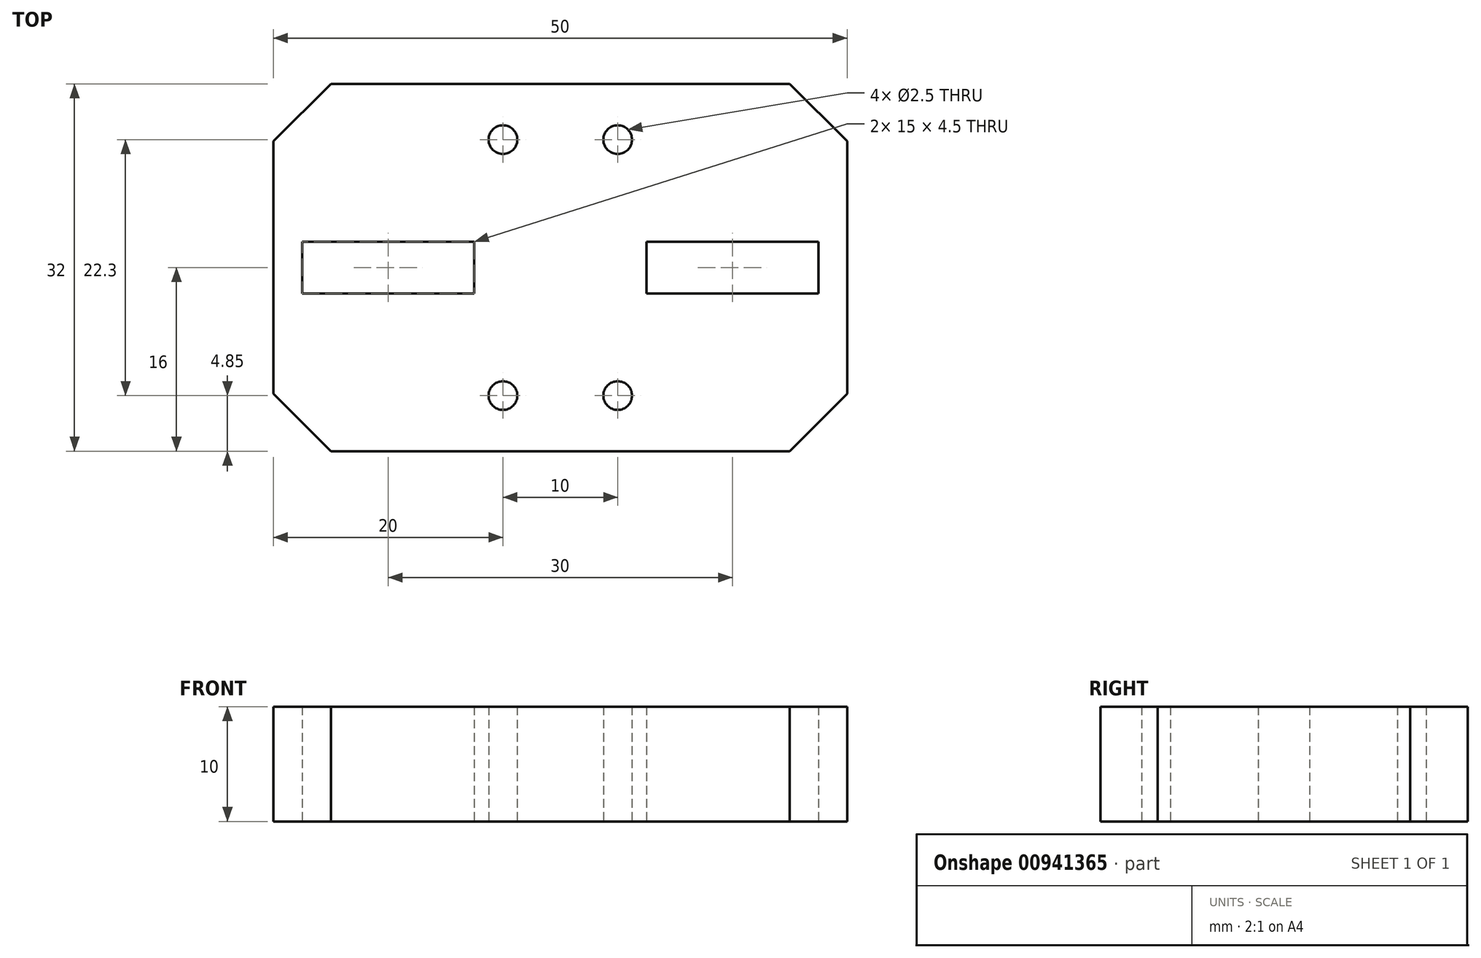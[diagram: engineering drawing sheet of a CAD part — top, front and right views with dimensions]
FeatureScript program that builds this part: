
annotation { "Feature Type Name" : "Feature", "Feature Type Description" : "" }
export const myFeature = defineFeature(function(context is Context, id is Id, definition is map)
    precondition{}
    {
        {
            var Q0;
            Q0=qCreatedBy(makeId("Top.planeOp"),FACE);
            var sketch = newSketch(context, id + "F0", { "sketchPlane" : qUnion([Q0])});
            skLineSegment(sketch, "E0.bottom", {"start": v(0, 0) * mm, "end": v(50, 0) * mm});
            skLineSegment(sketch, "E0.top", {"start": v(0, 32) * mm, "end": v(50, 32) * mm});
            skLineSegment(sketch, "E0.left", {"start": v(0, 0) * mm, "end": v(0, 32) * mm});
            skLineSegment(sketch, "E0.right", {"start": v(50, 0) * mm, "end": v(50, 32) * mm});
            skLineSegment(sketch, "E1", {"start": v(0, 16) * mm, "end": v(50, 16) * mm, "construction": true});
            skLineSegment(sketch, "E2.bottom", {"start": v(17.5, 18.25) * mm, "end": v(2.5, 18.25) * mm});
            skLineSegment(sketch, "E2.top", {"start": v(17.5, 13.75) * mm, "end": v(2.5, 13.75) * mm});
            skLineSegment(sketch, "E2.left", {"start": v(17.5, 18.25) * mm, "end": v(17.5, 13.75) * mm});
            skLineSegment(sketch, "E2.right", {"start": v(2.5, 18.25) * mm, "end": v(2.5, 13.75) * mm});
            skLineSegment(sketch, "E3", {"start": v(25, 32) * mm, "end": v(25, 0) * mm, "construction": true});
            skCircle(sketch, "E4", {"center": v(20, 27.15) * mm, "radius": 1.25 * mm});
            skCircle(sketch, "E5.MirrorC", {"center": v(30, 27.15) * mm, "radius": 1.25 * mm});
            skCircle(sketch, "E6.MirrorC", {"center": v(20, 4.85) * mm, "radius": 1.25 * mm});
            skCircle(sketch, "E7.MirrorC", {"center": v(30, 4.85) * mm, "radius": 1.25 * mm});
            skLineSegment(sketch, "E8.MirrorCS", {"start": v(32.5, 18.25) * mm, "end": v(32.5, 13.75) * mm});
            skLineSegment(sketch, "E9.MirrorCS", {"start": v(32.5, 18.25) * mm, "end": v(47.5, 18.25) * mm});
            skLineSegment(sketch, "E10.MirrorCS", {"start": v(47.5, 18.25) * mm, "end": v(47.5, 13.75) * mm});
            skLineSegment(sketch, "E11.MirrorCS", {"start": v(32.5, 13.75) * mm, "end": v(47.5, 13.75) * mm});
            skPoint(sketch, "E12", {"position": v(2.5, 16) * mm});
            skSolve(sketch);
        }
        {
            var Q0;
            Q0=makeQuery(id+"F0.imprint","IMPRINT",FACE,{"disambiguationData":[TD([[makeQuery(id+"F0.imprint","IMPRINT",EDGE,{"derivedFrom":sQuery(id+"F0.wireOp",EDGE,"E0.bottom")}),1.0]])]});
            extrude(context, id + "F1", {"entities" : qUnion([Q0]), "depth" : 10 * mm, "offsetDistance" : 25 * mm});
        }
        {
            var Q0;
            Q0=makeQuery(id+"F1.opExtrude","SWEPT_EDGE",EDGE,{"disambiguationData":[OSD([sQuery(id+"F0.wireOp",EDGE,"E0.bottom"),sQuery(id+"F0.wireOp",EDGE,"E0.left")])]});
            var Q1;
            Q1=makeQuery(id+"F1.opExtrude","SWEPT_EDGE",EDGE,{"disambiguationData":[OSD([sQuery(id+"F0.wireOp",EDGE,"E0.bottom"),sQuery(id+"F0.wireOp",EDGE,"E0.right")])]});
            var Q2;
            Q2=makeQuery(id+"F1.opExtrude","SWEPT_EDGE",EDGE,{"disambiguationData":[OSD([sQuery(id+"F0.wireOp",EDGE,"E0.top"),sQuery(id+"F0.wireOp",EDGE,"E0.right")])]});
            var Q3;
            Q3=makeQuery(id+"F1.opExtrude","SWEPT_EDGE",EDGE,{"disambiguationData":[OSD([sQuery(id+"F0.wireOp",EDGE,"E0.top"),sQuery(id+"F0.wireOp",EDGE,"E0.left")])]});
            chamfer(context, id + "F2", {"entities" : qUnion([Q0, Q1, Q2, Q3]), "width" : 5 * mm, "tangentPropagation" : true});
        }
    });
